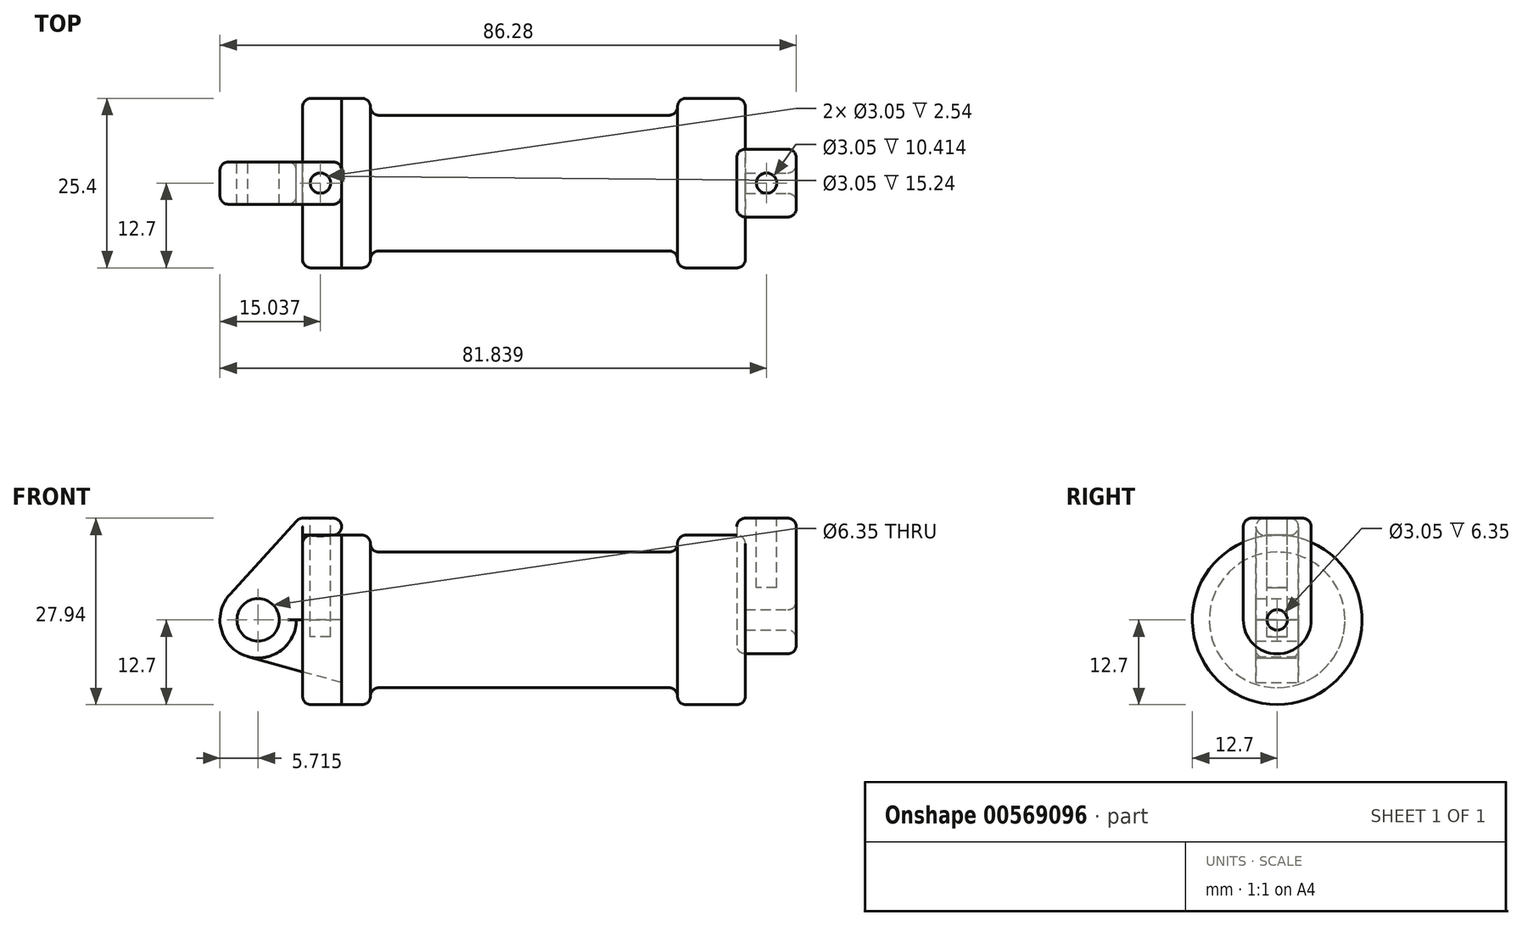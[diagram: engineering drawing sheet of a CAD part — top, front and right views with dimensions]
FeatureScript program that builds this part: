
annotation { "Feature Type Name" : "Feature", "Feature Type Description" : "" }
export const myFeature = defineFeature(function(context is Context, id is Id, definition is map)
    precondition{}
    {
        {
            var Q0;
            Q0=qCreatedBy(makeId("Front.planeOp"),FACE);
            var sketch = newSketch(context, id + "F0", { "sketchPlane" : qUnion([Q0])});
            skLineSegment(sketch, "E0", {"start": v(0, 0) * mm, "end": v(0, 12.7) * mm});
            skLineSegment(sketch, "E1", {"start": v(0, 12.7) * mm, "end": v(10.16, 12.7) * mm});
            skLineSegment(sketch, "E2", {"start": v(10.16, 12.7) * mm, "end": v(10.16, 10.16) * mm});
            skLineSegment(sketch, "E3", {"start": v(10.16, 10.16) * mm, "end": v(56.13, 10.16) * mm});
            skLineSegment(sketch, "E4", {"start": v(56.13, 10.16) * mm, "end": v(56.13, 12.7) * mm});
            skLineSegment(sketch, "E5", {"start": v(56.13, 12.7) * mm, "end": v(66.3, 12.7) * mm});
            skLineSegment(sketch, "E6", {"start": v(66.3, 12.7) * mm, "end": v(66.3, 0) * mm});
            skLineSegment(sketch, "E7", {"start": v(66.3, 0) * mm, "end": v(0, 0) * mm});
            skLineSegment(sketch, "E8", {"start": v(5.84, 15.24) * mm, "end": v(-0.5, 15.24) * mm});
            skLineSegment(sketch, "E9", {"start": v(-0.5, 15.24) * mm, "end": v(-10.88, 3.85) * mm});
            skLineSegment(sketch, "E10", {"start": v(0, 0) * mm, "end": v(-6.65, 0) * mm});
            skCircle(sketch, "E11", {"center": v(-6.65, 0) * mm, "radius": 5.72 * mm});
            skCircle(sketch, "E12", {"center": v(-6.65, 0) * mm, "radius": 3.18 * mm});
            skLineSegment(sketch, "E13", {"start": v(5.84, 15.24) * mm, "end": v(5.84, -9.4) * mm});
            skLineSegment(sketch, "E14", {"start": v(5.84, -9.4) * mm, "end": v(-8.18, -5.5) * mm});
            skSolve(sketch);
        }
        {
            var Q0;
            {var subQ1=sQuery(id+"F0.wireOp",EDGE,"E0");Q0=makeQuery(id+"F0.imprint","IMPRINT",FACE,{"disambiguationData":[TD([[makeQuery(id+"F0.imprint","IMPRINT",EDGE,{"derivedFrom":subQ1}),1.0]])]});}
            var Q1;
            {var subQ5=sQuery(id+"F0.wireOp",EDGE,"E12");Q1=makeQuery(id+"F0.imprint","IMPRINT",FACE,{"disambiguationData":[TD([[makeQuery(id+"F0.imprint","IMPRINT",EDGE,{"derivedFrom":subQ5}),-1.0]])]});}
            extrude(context, id + "F1", {"entities" : qUnion([Q0, Q1]), "endBound" : BoundingType.SYMMETRIC, "depth" : 6.35 * mm, "offsetDistance" : 25.4 * mm});
        }
        {
            var Q0;
            {var subQ0=sQuery(id+"F0.wireOp",EDGE,"E2");Q0=makeQuery(id+"F0.imprint","IMPRINT",FACE,{"disambiguationData":[TD([[makeQuery(id+"F0.imprint","IMPRINT",EDGE,{"derivedFrom":subQ0}),-1.0]])]});}
            var Q1;
            Q1=sQuery(id+"F0.wireOp",EDGE,"E7");
            revolve(context, id + "F2", {"entities" : qUnion([Q0]), "axis" : qUnion([Q1]), "revolveType" : RevolveType.FULL});
        }
        {
            var Q0;
            {var subQ0=sQuery(id+"F0.wireOp",EDGE,"E0");Q0=makeQuery(id+"F0.imprint","IMPRINT",FACE,{"disambiguationData":[TD([[makeQuery(id+"F0.imprint","IMPRINT",EDGE,{"derivedFrom":subQ0}),-1.0]])]});}
            var Q1;
            Q1=sQuery(id+"F0.wireOp",EDGE,"E7");
            revolve(context, id + "F3", {"entities" : qUnion([Q0]), "axis" : qUnion([Q1]), "revolveType" : RevolveType.FULL});
        }
        {
            var Q0;
            {var subQ0=sQuery(id+"F0.wireOp",EDGE,"E14");Q0=makeQuery(id+"F0.imprint","IMPRINT",FACE,{"disambiguationData":[TD([[makeQuery(id+"F0.imprint","IMPRINT",EDGE,{"derivedFrom":subQ0}),-1.0]])]});}
            extrude(context, id + "F4", {"entities" : qUnion([Q0]), "endBound" : BoundingType.SYMMETRIC, "depth" : 6.35 * mm, "offsetDistance" : 25.4 * mm});
        }
        {
            var Q0;
            Q0=makeQuery(id+"F2.opRevolve","SWEPT_FACE",FACE,{"disambiguationData":[OSD([sQuery(id+"F0.wireOp",EDGE,"E6")])]});
            var sketch = newSketch(context, id + "F5", { "sketchPlane" : qUnion([Q0])});
            skCircle(sketch, "E15", {"center": v(0, 0) * mm, "radius": 5.08 * mm});
            skCircle(sketch, "E16", {"center": v(0, 0) * mm, "radius": 1.52 * mm});
            skLineSegment(sketch, "E17", {"start": v(5.08, 0) * mm, "end": v(5.08, 15.24) * mm});
            skLineSegment(sketch, "E18", {"start": v(5.08, 15.24) * mm, "end": v(0, 15.24) * mm});
            skLineSegment(sketch, "E19", {"start": v(0, 15.24) * mm, "end": v(-5.08, 15.24) * mm});
            skLineSegment(sketch, "E20", {"start": v(-5.08, 15.24) * mm, "end": v(-5.08, 0) * mm});
            skSolve(sketch);
        }
        {
            var Q0;
            {var subQ4=sQuery(id+"F5.wireOp",EDGE,"E18");Q0=makeQuery(id+"F5.imprint","IMPRINT",FACE,{"disambiguationData":[TD([[makeQuery(id+"F5.imprint","IMPRINT",EDGE,{"derivedFrom":subQ4}),1.0]])]});}
            var Q1;
            {var subQ0=sQuery(id+"F5.wireOp",EDGE,"E17");var subQ1=sQuery(id+"F5.wireOp",EDGE,"E15");var subQ2=makeQuery(id+"F5.imprint","INTERSECT",VERTEX,{"derivedFrom":[subQ1,subQ0]});Q1=makeQuery(id+"F5.imprint","IMPRINT",FACE,{"disambiguationData":[TD([[makeQuery(id+"F5.imprint","IMPRINT",EDGE,{"disambiguationData":[TD([[subQ2,-1.0]])],"derivedFrom":subQ1}),-1.0]])]});}
            var Q2;
            Q2=makeQuery(id+"F5.imprint","IMPRINT",FACE,{"disambiguationData":[TD([[makeQuery(id+"F5.imprint","IMPRINT",EDGE,{"derivedFrom":sQuery(id+"F5.wireOp",EDGE,"E16")}),-1.0]])]});
            var Q3;
            Q3=makeQuery(id+"F5.imprint","IMPRINT",FACE,{"disambiguationData":[TD([[makeQuery(id+"F5.imprint","IMPRINT",EDGE,{"derivedFrom":sQuery(id+"F5.wireOp",EDGE,"E16")}),1.0]])]});
            extrude(context, id + "F6", {"entities" : qUnion([Q0, Q1, Q2, Q3]), "depth" : 7.62 * mm, "offsetDistance" : 25.4 * mm, "hasSecondDirection" : true, "secondDirectionOppositeDirection" : true, "secondDirectionDepth" : 1.27 * mm});
        }
        {
            var Q0;
            Q0=makeQuery(id+"F6.opExtrude","CAP_FACE",FACE,{"disambiguationData":[OSD([sQuery(id+"F5.wireOp",EDGE,"E15"),sQuery(id+"F5.wireOp",EDGE,"E17"),sQuery(id+"F5.wireOp",EDGE,"E18"),sQuery(id+"F5.wireOp",EDGE,"E19"),sQuery(id+"F5.wireOp",EDGE,"E20")])],"isStart":false});
            var sketch = newSketch(context, id + "F7", { "sketchPlane" : qUnion([Q0])});
            skCircle(sketch, "E21", {"center": v(0, 0) * mm, "radius": 1.52 * mm});
            skSolve(sketch);
        }
        {
            var Q0;
            Q0=makeQuery(id+"F7.imprint","IMPRINT",FACE,{"disambiguationData":[TD([[makeQuery(id+"F7.imprint","IMPRINT",EDGE,{"derivedFrom":sQuery(id+"F7.wireOp",EDGE,"E21")}),1.0]])]});
            extrude(context, id + "F8", {"entities" : qUnion([Q0]), "operationType" : NewBodyOperationType.REMOVE, "oppositeDirection" : true, "depth" : 7.62 * mm, "offsetDistance" : 25.4 * mm});
        }
        {
            var Q0;
            Q0=makeQuery(id+"F1.opExtrude","SWEPT_FACE",FACE,{"disambiguationData":[OSD([sQuery(id+"F0.wireOp",EDGE,"E8")])]});
            var sketch = newSketch(context, id + "F9", { "sketchPlane" : qUnion([Q0])});
            skCircle(sketch, "E22", {"center": v(2.67, 0) * mm, "radius": 1.52 * mm});
            skSolve(sketch);
        }
        {
            var Q0;
            Q0=makeQuery(id+"F6.opExtrude","SWEPT_FACE",FACE,{"disambiguationData":[OSD([sQuery(id+"F5.wireOp",EDGE,"E18"),sQuery(id+"F5.wireOp",EDGE,"E19")])]});
            var sketch = newSketch(context, id + "F10", { "sketchPlane" : qUnion([Q0])});
            skCircle(sketch, "E23", {"center": v(69.47, 0) * mm, "radius": 1.52 * mm});
            skSolve(sketch);
        }
        {
            var Q0;
            Q0=makeQuery(id+"F9.imprint","IMPRINT",FACE,{"disambiguationData":[TD([[makeQuery(id+"F9.imprint","IMPRINT",EDGE,{"derivedFrom":sQuery(id+"F9.wireOp",EDGE,"E22")}),1.0]])]});
            extrude(context, id + "F11", {"entities" : qUnion([Q0]), "operationType" : NewBodyOperationType.REMOVE, "oppositeDirection" : true, "depth" : 17.78 * mm, "offsetDistance" : 25.4 * mm});
        }
        {
            var Q0;
            Q0=makeQuery(id+"F10.imprint","IMPRINT",FACE,{"disambiguationData":[TD([[makeQuery(id+"F10.imprint","IMPRINT",EDGE,{"derivedFrom":sQuery(id+"F10.wireOp",EDGE,"E23")}),1.0]])]});
            extrude(context, id + "F12", {"entities" : qUnion([Q0]), "operationType" : NewBodyOperationType.REMOVE, "oppositeDirection" : true, "depth" : 10.4 * mm, "offsetDistance" : 25.4 * mm});
        }
        {
            var Q0;
            Q0=makeQuery(id+"F2.opRevolve","SWEPT_EDGE",EDGE,{"disambiguationData":[OSD([sQuery(id+"F0.wireOp",EDGE,"E1"),sQuery(id+"F0.wireOp",EDGE,"E2")])]});
            var Q1;
            Q1=makeQuery(id+"F2.opRevolve","SWEPT_EDGE",EDGE,{"disambiguationData":[OSD([sQuery(id+"F0.wireOp",EDGE,"E2"),sQuery(id+"F0.wireOp",EDGE,"E3")])]});
            var Q2;
            Q2=makeQuery(id+"F3.opRevolve","SWEPT_EDGE",EDGE,{"disambiguationData":[OSD([sQuery(id+"F0.wireOp",EDGE,"E0"),sQuery(id+"F0.wireOp",EDGE,"E1")])]});
            var Q3;
            Q3=makeQuery(id+"F2.opRevolve","SWEPT_EDGE",EDGE,{"disambiguationData":[OSD([sQuery(id+"F0.wireOp",EDGE,"E4"),sQuery(id+"F0.wireOp",EDGE,"E5")])]});
            var Q4;
            Q4=makeQuery(id+"F2.opRevolve","SWEPT_EDGE",EDGE,{"disambiguationData":[OSD([sQuery(id+"F0.wireOp",EDGE,"E5"),sQuery(id+"F0.wireOp",EDGE,"E6")])]});
            var Q5;
            Q5=makeQuery(id+"F2.opRevolve","SWEPT_EDGE",EDGE,{"disambiguationData":[OSD([sQuery(id+"F0.wireOp",EDGE,"E3"),sQuery(id+"F0.wireOp",EDGE,"E4")])]});
            fillet(context, id + "F13", {"entities" : qUnion([Q0, Q1, Q2, Q3, Q4, Q5]), "radius" : 1.27 * mm, "tangentPropagation" : true, "allowEdgeOverflow" : false});
        }
        {
            var Q0;
            Q0=makeQuery(id+"F6.opExtrude","CAP_EDGE",EDGE,{"disambiguationData":[OSD([sQuery(id+"F5.wireOp",EDGE,"E20")])],"isStart":false});
            var Q1;
            Q1=makeQuery(id+"F6.opExtrude","CAP_EDGE",EDGE,{"disambiguationData":[OSD([sQuery(id+"F5.wireOp",EDGE,"E18"),sQuery(id+"F5.wireOp",EDGE,"E19")])],"isStart":false});
            var Q2;
            Q2=makeQuery(id+"F6.opExtrude","CAP_EDGE",EDGE,{"disambiguationData":[OSD([sQuery(id+"F5.wireOp",EDGE,"E17")])],"isStart":false});
            var Q3;
            Q3=makeQuery(id+"F6.opExtrude","CAP_FACE",FACE,{"disambiguationData":[OSD([sQuery(id+"F5.wireOp",EDGE,"E15"),sQuery(id+"F5.wireOp",EDGE,"E17"),sQuery(id+"F5.wireOp",EDGE,"E18"),sQuery(id+"F5.wireOp",EDGE,"E19"),sQuery(id+"F5.wireOp",EDGE,"E20")])],"isStart":false});
            var Q4;
            Q4=makeQuery(id+"F6.opExtrude","CAP_EDGE",EDGE,{"disambiguationData":[OSD([sQuery(id+"F5.wireOp",EDGE,"E20")])],"isStart":true});
            var Q5;
            Q5=makeQuery(id+"F6.opExtrude","SWEPT_EDGE",EDGE,{"disambiguationData":[OSD([sQuery(id+"F5.wireOp",EDGE,"E19"),sQuery(id+"F5.wireOp",EDGE,"E20")])]});
            var Q6;
            Q6=makeQuery(id+"F6.opExtrude","CAP_EDGE",EDGE,{"disambiguationData":[OSD([sQuery(id+"F5.wireOp",EDGE,"E18"),sQuery(id+"F5.wireOp",EDGE,"E19")])],"isStart":true});
            var Q7;
            Q7=makeQuery(id+"F6.opExtrude","SWEPT_FACE",FACE,{"disambiguationData":[OSD([sQuery(id+"F5.wireOp",EDGE,"E17")])]});
            fillet(context, id + "F14", {"entities" : qUnion([Q0, Q1, Q2, Q3, Q4, Q5, Q6, Q7]), "radius" : 1.27 * mm, "tangentPropagation" : true, "allowEdgeOverflow" : false});
        }
        {
            var Q0;
            Q0=makeQuery(id+"F1.opExtrude","CAP_EDGE",EDGE,{"disambiguationData":[OSD([sQuery(id+"F0.wireOp",EDGE,"E9")])],"isStart":false});
            var Q1;
            Q1=makeQuery(id+"F1.opExtrude","CAP_EDGE",EDGE,{"disambiguationData":[OSD([sQuery(id+"F0.wireOp",EDGE,"E8")])],"isStart":false});
            var Q2;
            Q2=makeQuery(id+"F1.opExtrude","SWEPT_EDGE",EDGE,{"disambiguationData":[OSD([sQuery(id+"F0.wireOp",EDGE,"E8"),sQuery(id+"F0.wireOp",EDGE,"E13")])]});
            var Q3;
            Q3=makeQuery(id+"F1.opExtrude","SWEPT_EDGE",EDGE,{"disambiguationData":[OSD([sQuery(id+"F0.wireOp",EDGE,"E8"),sQuery(id+"F0.wireOp",EDGE,"E9")])]});
            var Q4;
            Q4=makeQuery(id+"F1.opExtrude","CAP_EDGE",EDGE,{"disambiguationData":[OSD([sQuery(id+"F0.wireOp",EDGE,"E9")])],"isStart":true});
            var Q5;
            Q5=makeQuery(id+"F1.opExtrude","CAP_EDGE",EDGE,{"disambiguationData":[OSD([sQuery(id+"F0.wireOp",EDGE,"E8")])],"isStart":true});
            fillet(context, id + "F15", {"entities" : qUnion([Q0, Q1, Q2, Q3, Q4, Q5]), "radius" : 1.27 * mm, "tangentPropagation" : true, "allowEdgeOverflow" : false});
        }
        {
            var Q0;
            Q0=makeQuery(id+"F1.opExtrude","CAP_EDGE",EDGE,{"disambiguationData":[OSD([sQuery(id+"F0.wireOp",EDGE,"E1")])],"isStart":false});
            var Q1;
            Q1=makeQuery(id+"F1.opExtrude","SWEPT_FACE",FACE,{"disambiguationData":[OSD([sQuery(id+"F0.wireOp",EDGE,"E13")])]});
            var Q2;
            Q2=makeQuery(id+"F1.opExtrude","CAP_EDGE",EDGE,{"disambiguationData":[OSD([sQuery(id+"F0.wireOp",EDGE,"E1")])],"isStart":true});
            fillet(context, id + "F16", {"entities" : qUnion([Q0, Q1, Q2]), "radius" : 1.27 * mm, "tangentPropagation" : true, "allowEdgeOverflow" : false});
        }
    });
